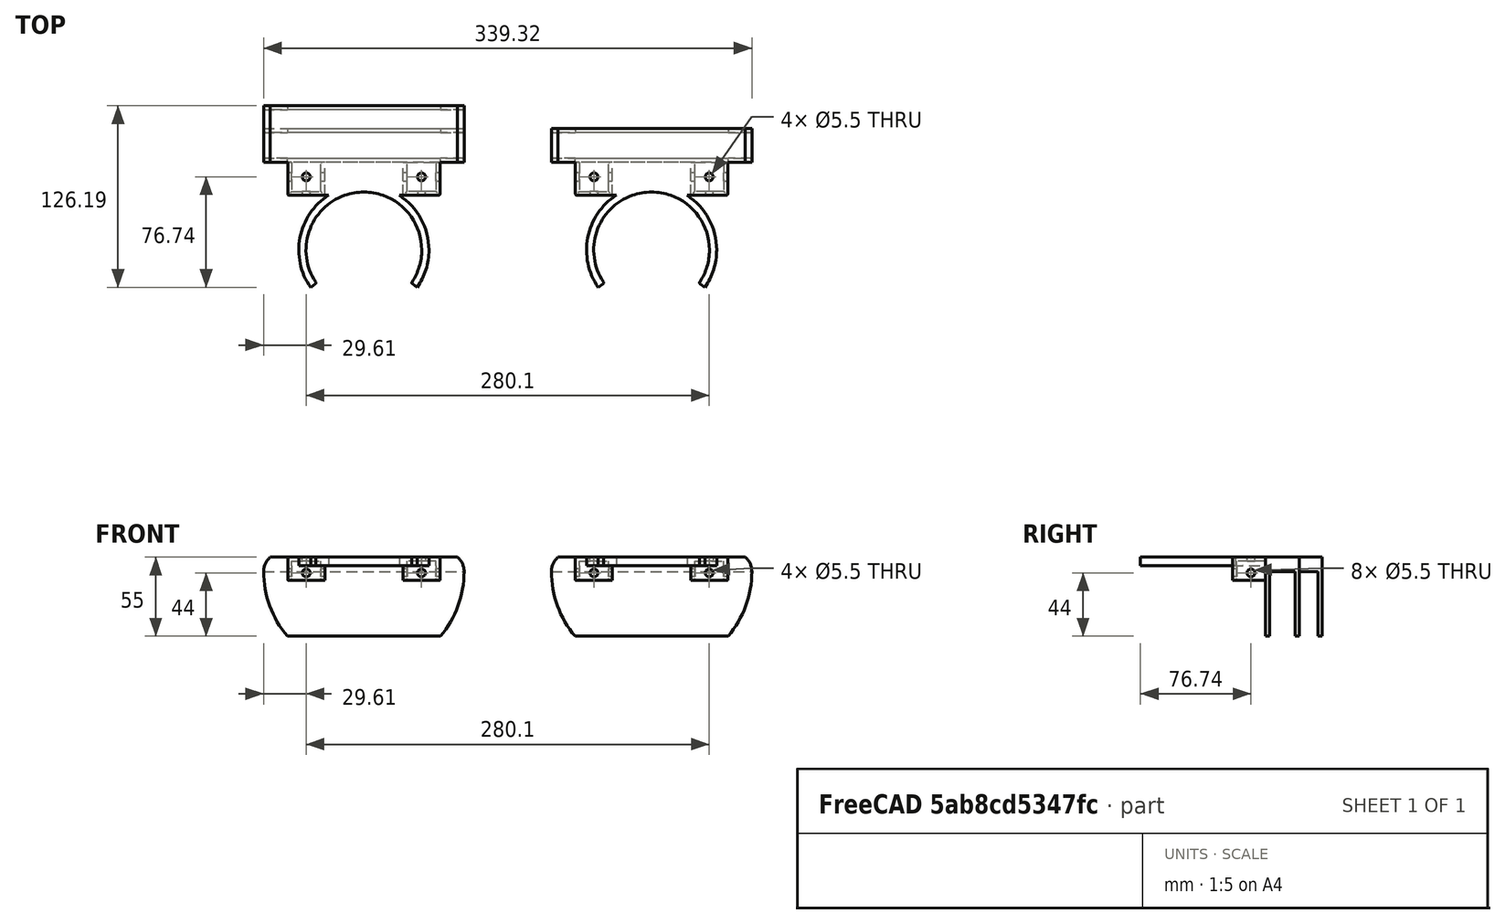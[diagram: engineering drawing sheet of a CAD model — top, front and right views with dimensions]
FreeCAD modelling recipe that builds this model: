
FCSTD DOCUMENT  (FreeCAD 0.19R21775 (Git))
Label: parts - RC1
License: All rights reserved
LicenseURL: http://en.wikipedia.org/wiki/All_rights_reserved
objects: TechDraw::DrawViewDimension×74, Sketcher::SketchObject×20, PartDesign::Pad×12, PartDesign::Pocket×12, TechDraw::DrawViewPart×6, PartDesign::Fillet×4, Spreadsheet::Sheet×2, PartDesign::Body×2, TechDraw::DrawSVGTemplate×2, TechDraw::DrawPage×2, Mesh::Feature×2
note: 78 computed .brp shape members not serialized (recipe doc carries the construction recipe); baked Part::Feature solids carry a one-line shape summary decoded from their .brp

FEATURE [Sketcher::SketchObject] Sketch036
  MapMode = 5
  Support = -> [XY_Plane006]
  expr: Constraints[8] = Spreadsheet006.pillar
  expr: Constraints[6] = Spreadsheet006.pillar / 2 - Spreadsheet006.offset
  expr: Constraints[5] = Spreadsheet006.wall + Spreadsheet006.gap / 2 + Spreadsheet006.extrusion
  expr: Constraints[10] = Spreadsheet006.pillar + 10mm
  sketch-geometry (4):
    g0: LineSegment [constr] StartX=52.9 StartY=0 StartZ=0 EndX=52.9 EndY=-37.955 EndZ=0
    g1: LineSegment [constr] StartX=52.9 StartY=-37.955 StartZ=0 EndX=0 EndY=-37.955 EndZ=0
    g2: Circle CenterX=52.9 CenterY=-37.955 CenterZ=0 NormalX=0 NormalY=0 NormalZ=1 AngleXU=0 Radius=40.225
    g3: Circle CenterX=52.9 CenterY=-37.955 CenterZ=0 NormalX=0 NormalY=0 NormalZ=1 AngleXU=0 Radius=45.225
  constraints (11):
    c: PointOnObject(g0,g-1)
    c: Vertical(g0)
    c: Coincident(g1,g0)
    c: PointOnObject(g1,g-2)
    c: Horizontal(g1)
    c: Distance(g1) = 52.9
    c: Distance(g0) = 37.955
    c: Coincident(g2,g0)
    c: Diameter(g2) = 80.45
    c: Coincident(g3,g2)
    c: Diameter(g3) = 90.45
FEATURE [Sketcher::SketchObject] Sketch038
  MapMode = 5
  Support = -> [XY_Plane006]
  expr: Constraints[25] = Spreadsheet006.wall
  expr: Constraints[26] = Spreadsheet006.wall
  expr: Constraints[28] = Spreadsheet006.wall
  expr: Constraints[29] = Spreadsheet006.wall
  expr: Constraints[27] = Spreadsheet006.wall
  expr: Constraints[30] = Spreadsheet006.gap
  expr: Constraints[31] = Spreadsheet006.extrusion
  sketch-geometry (12):
    g0: LineSegment StartX=0 StartY=0 StartZ=0 EndX=105.8 EndY=0 EndZ=0
    g1: LineSegment StartX=105.8 StartY=0 StartZ=0 EndX=105.8 EndY=25.7 EndZ=0
    g2: LineSegment StartX=105.8 StartY=25.7 StartZ=0 EndX=0 EndY=25.7 EndZ=0
    g3: LineSegment StartX=0 StartY=25.7 StartZ=0 EndX=0 EndY=0 EndZ=0
    g4: LineSegment StartX=2.8 StartY=22.9 StartZ=0 EndX=22.9 EndY=22.9 EndZ=0
    g5: LineSegment StartX=22.9 StartY=22.9 StartZ=0 EndX=22.9 EndY=2.8 EndZ=0
    g6: LineSegment StartX=22.9 StartY=2.8 StartZ=0 EndX=2.8 EndY=2.8 EndZ=0
    g7: LineSegment StartX=2.8 StartY=2.8 StartZ=0 EndX=2.8 EndY=22.9 EndZ=0
    g8: LineSegment StartX=82.9 StartY=22.9 StartZ=0 EndX=103 EndY=22.9 EndZ=0
    g9: LineSegment StartX=103 StartY=22.9 StartZ=0 EndX=103 EndY=2.8 EndZ=0
    g10: LineSegment StartX=103 StartY=2.8 StartZ=0 EndX=82.9 EndY=2.8 EndZ=0
    g11: LineSegment StartX=82.9 StartY=2.8 StartZ=0 EndX=82.9 EndY=22.9 EndZ=0
  constraints (35):
    c: Coincident(g0,g1)
    c: Coincident(g1,g2)
    c: Coincident(g2,g3)
    c: Coincident(g3,g0)
    c: Horizontal(g0)
    c: Horizontal(g2)
    c: Vertical(g1)
    c: Vertical(g3)
    c: Coincident(g0,g-1)
    c: Coincident(g4,g5)
    c: Coincident(g5,g6)
    c: Coincident(g6,g7)
    c: Coincident(g7,g4)
    c: Horizontal(g4)
    c: Horizontal(g6)
    c: Vertical(g5)
    c: Vertical(g7)
    c: Coincident(g8,g9)
    c: Coincident(g9,g10)
    c: Coincident(g10,g11)
    c: Coincident(g11,g8)
    c: Horizontal(g8)
    c: Horizontal(g10)
    c: Vertical(g9)
    c: Vertical(g11)
    c: Distance(g5,g0) = 2.8
    c: Distance(g4,g2) = 2.8
    c: Distance(g6,g3) = 2.8
    c: Distance(g8,g2) = 2.8
    c: Distance(g9,g1) = 2.8
    c: Distance(g4,g8) = 60
    c: Distance(g4) = 20.1
    c: Equal(g4,g5)
    c: Equal(g5,g11)
    c: Equal(g4,g8)
FEATURE [PartDesign::Pad] Pad020
  Length = 6
  Length2 = 100
  Profile = -> Sketch038
  Type = 0
  expr: Length = Spreadsheet006.height
FEATURE [PartDesign::Pad] Pad019
  BaseFeature = -> Pad020
  Length = 6
  Length2 = 100
  Profile = -> Sketch036
  Type = 0
  expr: Length = Spreadsheet006.height
FEATURE [PartDesign::Pocket] Pocket020
  BaseFeature = -> Pad019
  Length = 6
  Length2 = 100
  Profile = -> Pad019 [Face25]
  Type = 0
  expr: Length = Spreadsheet006.height
FEATURE [Spreadsheet::Sheet] Spreadsheet006  label="Data Laptop Holder - One Slot Closed"
  cells = A1=Extrusion width; B1(extrusion)==20.1mm; A2=wall thinkness; B2(wall)==2.8mm; A3=Gap; B3(gap)==60mm; A4=height; B4(height)==6mm; A5=Pillar; B5(pillar)==80.45mm; A6=offset; B6(offset)==2.27mm; A7=cake; B7(cake)==110deg; A8=Socket Height; B8(socketheight)==10mm; A9=Fix Hole Diameter; B9(fixholedia)==5.5mm; A10=Block; A11=Depth; B11(block_depth)==gap + 70mm; A12=Laptop Height; B12(block_mbp)==18mm; C12=Adjust laptop height here; A13=Overhang; B13(block_overhang)==50deg; A14=Support Sidewall; B14(block_sidewall)==3mm; A15=New Height; B15(block_height)==10mm; A16=New Support Height; B16(block_newsupportheight)==45mm
FEATURE [Sketcher::SketchObject] Sketch039
  MapMode = 5
  Support = -> [XY_Plane006]
  expr: Constraints[5] = Spreadsheet006.pillar / 2 - Spreadsheet006.offset
  expr: Constraints[6] = Spreadsheet006.wall + Spreadsheet006.extrusion + Spreadsheet006.gap / 2
  expr: Constraints[14] = Spreadsheet006.cake / 2
  expr: Constraints[7] = Spreadsheet006.pillar + 20mm
  expr: Constraints[19] = Spreadsheet006.cake
  sketch-geometry (7):
    g0: LineSegment [constr] StartX=52.9 StartY=0 StartZ=0 EndX=52.9 EndY=-37.955 EndZ=0
    g1: LineSegment [constr] StartX=52.9 StartY=-37.955 StartZ=0 EndX=0 EndY=-37.955 EndZ=0
    g2: Circle [constr] CenterX=52.9 CenterY=-37.955 CenterZ=0 NormalX=0 NormalY=0 NormalZ=1 AngleXU=0 Radius=50.225
    g3: LineSegment [constr] StartX=52.9 StartY=-37.955 StartZ=0 EndX=52.9 EndY=-88.18 EndZ=0
    g4: LineSegment StartX=52.9 StartY=-37.955 StartZ=0 EndX=94.0419 EndY=-66.7629 EndZ=0
    g5: LineSegment StartX=52.9 StartY=-37.955 StartZ=0 EndX=11.7581 EndY=-66.7629 EndZ=0
    g6: ArcOfCircle CenterX=52.9 CenterY=-37.955 CenterZ=0 NormalX=0 NormalY=0 NormalZ=1 AngleXU=0 Radius=50.225 StartAngle=3.75246 EndAngle=5.67232
  constraints (20):
    c: PointOnObject(g0,g-1)
    c: Vertical(g0)
    c: Coincident(g1,g0)
    c: PointOnObject(g1,g-2)
    c: Horizontal(g1)
    c: Distance(g0) = 37.955
    c: Distance(g1) = 52.9
    c: Diameter(g2) = 100.45
    c: Coincident(g2,g0)
    c: Coincident(g3,g0)
    c: PointOnObject(g3,g2)
    c: Vertical(g3)
    c: Coincident(g4,g0)
    c: PointOnObject(g4,g2)
    c: Angle(g3,g4) = 0.959931
    c: Coincident(g5,g4)
    c: Coincident(g6,g4)
    c: Coincident(g6,g4)
    c: Coincident(g6,g5)
    c: Angle(g5,g4) = 1.91986
FEATURE [PartDesign::Pocket] Pocket021
  BaseFeature = -> Pocket020
  Length = 6
  Length2 = 100
  Profile = -> Sketch039
  Reversed = true
  Type = 0
  expr: Length = Spreadsheet006.height
FEATURE [PartDesign::Fillet] Fillet008
  Base = -> Pocket021 [Edge51,Edge71]
  BaseFeature = -> Pocket021
  Radius = 1
  SupportTransform = true
FEATURE [Sketcher::SketchObject] Sketch034
  ExternalGeometry = -> [Fillet008]
  MapMode = 5
  Placement = pos=(0,0,0) rot=(1,0,0;3.14159rad)
  Support = -> [Fillet008]
  expr: Constraints[40] = Spreadsheet006.wall * 2 + Spreadsheet006.extrusion
  expr: Constraints[41] = Spreadsheet006.wall * 2 + Spreadsheet006.extrusion
  sketch-geometry (16):
    g0: LineSegment StartX=2.8 StartY=-2.8 StartZ=0 EndX=22.9 EndY=-2.8 EndZ=0
    g1: LineSegment StartX=22.9 StartY=-2.8 StartZ=0 EndX=22.9 EndY=-22.9 EndZ=0
    g2: LineSegment StartX=22.9 StartY=-22.9 StartZ=0 EndX=2.8 EndY=-22.9 EndZ=0
    g3: LineSegment StartX=2.8 StartY=-22.9 StartZ=0 EndX=2.8 EndY=-2.8 EndZ=0
    g4: LineSegment StartX=82.9 StartY=-22.9 StartZ=0 EndX=103 EndY=-22.9 EndZ=0
    g5: LineSegment StartX=103 StartY=-22.9 StartZ=0 EndX=103 EndY=-2.8 EndZ=0
    g6: LineSegment StartX=103 StartY=-2.8 StartZ=0 EndX=82.9 EndY=-2.8 EndZ=0
    g7: LineSegment StartX=82.9 StartY=-2.8 StartZ=0 EndX=82.9 EndY=-22.9 EndZ=0
    g8: LineSegment StartX=0 StartY=0 StartZ=0 EndX=25.7 EndY=0 EndZ=0
    g9: LineSegment StartX=25.7 StartY=0 StartZ=0 EndX=25.7 EndY=-25.7 EndZ=0
    g10: LineSegment StartX=25.7 StartY=-25.7 StartZ=0 EndX=0 EndY=-25.7 EndZ=0
    g11: LineSegment StartX=0 StartY=-25.7 StartZ=0 EndX=0 EndY=0 EndZ=0
    g12: LineSegment StartX=105.8 StartY=0 StartZ=0 EndX=80.1 EndY=0 EndZ=0
    g13: LineSegment StartX=80.1 StartY=0 StartZ=0 EndX=80.1 EndY=-25.7 EndZ=0
    g14: LineSegment StartX=80.1 StartY=-25.7 StartZ=0 EndX=105.8 EndY=-25.7 EndZ=0
    g15: LineSegment StartX=105.8 StartY=-25.7 StartZ=0 EndX=105.8 EndY=0 EndZ=0
  constraints (42):
    c: Coincident(g0,g1)
    c: Coincident(g1,g2)
    c: Coincident(g2,g3)
    c: Coincident(g3,g0)
    c: Horizontal(g0)
    c: Horizontal(g2)
    c: Vertical(g1)
    c: Vertical(g3)
    c: Coincident(g0,g-6)
    c: Coincident(g1,g-7)
    c: Coincident(g4,g5)
    c: Coincident(g5,g6)
    c: Coincident(g6,g7)
    c: Coincident(g7,g4)
    c: Horizontal(g4)
    c: Horizontal(g6)
    c: Vertical(g5)
    c: Vertical(g7)
    c: Coincident(g4,g-4)
    c: Coincident(g5,g-3)
    c: Coincident(g8,g9)
    c: Coincident(g9,g10)
    c: Coincident(g10,g11)
    c: Coincident(g11,g8)
    c: Horizontal(g8)
    c: Horizontal(g10)
    c: Vertical(g9)
    c: Vertical(g11)
    c: Coincident(g8,g-1)
    c: PointOnObject(g9,g-8)
    c: Coincident(g12,g13)
    c: Coincident(g13,g14)
    c: Coincident(g14,g15)
    c: Coincident(g15,g12)
    c: Horizontal(g12)
    c: Horizontal(g14)
    c: Vertical(g13)
    c: Vertical(g15)
    c: Coincident(g12,g-5)
    c: PointOnObject(g13,g-8)
    c: Distance(g10) = 25.7
    c: Distance(g14) = 25.7
FEATURE [PartDesign::Pad] Pad021
  BaseFeature = -> Fillet008
  Length = 10
  Length2 = 100
  Profile = -> Sketch034
  Type = 0
  expr: Length = Spreadsheet006.socketheight
FEATURE [Sketcher::SketchObject] Sketch033
  ExternalGeometry = -> [Pad021]
  MapMode = 5
  Placement = pos=(0,0,0) rot=(0.57735,-0.57735,-0.57735;2.0944rad)
  Support = -> [Pad021]
  expr: Constraints[0] = Spreadsheet006.wall + 0.5 * Spreadsheet006.extrusion
  expr: Constraints[1] = Spreadsheet006.socketheight / 2
  expr: Constraints[2] = Spreadsheet006.fixholedia
  sketch-geometry (1):
    g0: Circle CenterX=-12.85 CenterY=-5 CenterZ=0 NormalX=0 NormalY=0 NormalZ=1 AngleXU=0 Radius=2.75
  constraints (3):
    c: Distance(g0,g-4) = 12.85
    c: Distance(g0,g-3) = 5
    c: Diameter(g0) = 5.5
FEATURE [PartDesign::Pocket] Pocket024
  BaseFeature = -> Pad021
  Length = 105.8
  Length2 = 100
  Profile = -> Sketch033
  Type = 0
  expr: Length = Spreadsheet006.gap + 2 * (Spreadsheet006.wall + Spreadsheet006.extrusion)
FEATURE [Sketcher::SketchObject] Sketch040
  ExternalGeometry = -> [Pocket024]
  MapMode = 5
  Placement = pos=(0,0,0) rot=(1,0,0;1.5708rad)
  Support = -> [Pocket024]
  expr: Constraints[0] = Spreadsheet006.wall + 0.5 * Spreadsheet006.extrusion
  expr: Constraints[1] = Spreadsheet006.wall + 0.5 * Spreadsheet006.extrusion
  expr: Constraints[3] = Spreadsheet006.socketheight / 2
  expr: Constraints[2] = Spreadsheet006.socketheight / 2
  expr: Constraints[4] = Spreadsheet006.fixholedia
  sketch-geometry (2):
    g0: Circle CenterX=12.85 CenterY=-5 CenterZ=0 NormalX=0 NormalY=0 NormalZ=1 AngleXU=0 Radius=2.75
    g1: Circle CenterX=92.95 CenterY=-5 CenterZ=0 NormalX=0 NormalY=0 NormalZ=1 AngleXU=0 Radius=2.75
  constraints (6):
    c: Distance(g0,g-5) = 12.85
    c: Distance(g1,g-4) = 12.85
    c: Distance(g0,g-6) = 5
    c: Distance(g1,g-3) = 5
    c: Diameter(g0) = 5.5
    c: Equal(g0,g1)
FEATURE [PartDesign::Pocket] Pocket023
  BaseFeature = -> Pocket024
  Length = 2.8
  Length2 = 100
  Profile = -> Sketch040
  Type = 0
  expr: Length = Spreadsheet006.wall
FEATURE [PartDesign::Fillet] Fillet009
  Base = -> Pocket023 [Edge114,Edge113,Edge112,Edge85,Edge86,Edge83,Edge37,Edge22,Edge108,Edge70]
  BaseFeature = -> Pocket023
  Radius = 1
  SupportTransform = true
FEATURE [Sketcher::SketchObject] Sketch037
  ExternalGeometry = -> [Fillet009]
  MapMode = 5
  Placement = pos=(0,25.7,0) rot=(0,0.707107,0.707107;3.14159rad)
  Support = -> [Fillet009]
  expr: Constraints[7] = Spreadsheet006.block_depth / 2
  expr: Constraints[5] = Spreadsheet006.block_height
  expr: Constraints[16] = 180deg - Spreadsheet006.block_overhang
  expr: Constraints[10] = 180deg - Spreadsheet006.block_overhang
  expr: Constraints[3] = (Spreadsheet006.block_depth - (Spreadsheet006.gap + 2 * (Spreadsheet006.wall + Spreadsheet006.extrusion))) / 2
  expr: Constraints[6] = 2 * Spreadsheet006.block_depth
  expr: Constraints[2] = Spreadsheet006.block_depth
  sketch-geometry (7):
    g0: LineSegment StartX=12.1 StartY=6 StartZ=0 EndX=-117.9 EndY=6 EndZ=0
    g1: LineSegment [constr] StartX=-182.9 StartY=-4 StartZ=0 EndX=77.1 EndY=-4 EndZ=0
    g2: LineSegment [constr] StartX=-117.9 StartY=6 StartZ=0 EndX=-109.509 EndY=-4 EndZ=0
    g3: ArcOfCircle CenterX=-109.509 CenterY=-4 CenterZ=0 NormalX=0 NormalY=0 NormalZ=1 AngleXU=0 Radius=13.0541 StartAngle=2.26893 EndAngle=3.14159
    g4: LineSegment [constr] StartX=12.1 StartY=6 StartZ=0 EndX=3.709 EndY=-4 EndZ=0
    g5: ArcOfCircle CenterX=3.709 CenterY=-4 CenterZ=0 NormalX=0 NormalY=0 NormalZ=1 AngleXU=0 Radius=13.0541 StartAngle=2.9155e-12 EndAngle=0.872665
    g6: ArcOfCircle CenterX=-52.9 CenterY=-4 CenterZ=0 NormalX=0 NormalY=0 NormalZ=1 AngleXU=0 Radius=69.6631 StartAngle=3.14159 EndAngle=6.28319
  constraints (23):
    c: Horizontal(g0)
    c: PointOnObject(g-4,g0)
    c: Distance(g0) = 130
    c: Distance(g0,g-5) = 12.1
    c: Horizontal(g1)
    c: Distance(g0,g1) = 10
    c: Distance(g1) = 260
    c: DistanceX(g1,g0) = 65
    c: Coincident(g2,g0)
    c: PointOnObject(g2,g1)
    c: Angle(g1,g2) = 2.26893
    c: Coincident(g3,g2)
    c: Coincident(g3,g0)
    c: PointOnObject(g3,g1)
    c: Coincident(g4,g0)
    c: PointOnObject(g4,g1)
    c: Angle(g4,g1) = 2.26893
    c: Coincident(g5,g4)
    c: Coincident(g5,g0)
    c: PointOnObject(g5,g1)
    c: PointOnObject(g6,g1)
    c: Coincident(g6,g3)
    c: Coincident(g6,g5)
FEATURE [PartDesign::Pad] Pad022
  BaseFeature = -> Fillet009
  Length = 20.8
  Length2 = 100
  Profile = -> Sketch037
  Type = 0
  expr: Length = Spreadsheet006.block_mbp + Spreadsheet006.wall
FEATURE [PartDesign::Pad] Pad018
  BaseFeature = -> Pad022
  Length = 2.8
  Length2 = 100
  Profile = -> Pad022 [Face4]
  Type = 0
  expr: Length = Spreadsheet006.wall
FEATURE [Sketcher::SketchObject] Sketch041
  AttachmentOffset = pos=(0,0,-49) rot=(0,0,1;0rad)
  ExternalGeometry = -> [Pad018]
  MapMode = 5
  Placement = pos=(0,0,-49) rot=(0,0,1;0rad)
  Support = -> [XY_Plane006]
  expr: .AttachmentOffset.Base.z = -1 * (Spreadsheet006.block_newsupportheight + Spreadsheet006.block_height - Spreadsheet006.height)
  sketch-geometry (4):
    g0: LineSegment StartX=-16.7631 StartY=46.5 StartZ=0 EndX=122.563 EndY=46.5 EndZ=0
    g1: LineSegment StartX=122.563 StartY=46.5 StartZ=0 EndX=122.563 EndY=0 EndZ=0
    g2: LineSegment StartX=122.563 StartY=0 StartZ=0 EndX=-16.7631 EndY=0 EndZ=0
    g3: LineSegment StartX=-16.7631 StartY=0 StartZ=0 EndX=-16.7631 EndY=46.5 EndZ=0
  constraints (10):
    c: Coincident(g0,g1)
    c: Coincident(g1,g2)
    c: Coincident(g2,g3)
    c: Coincident(g3,g0)
    c: Horizontal(g2)
    c: Vertical(g1)
    c: Vertical(g3)
    c: Coincident(g0,g-5)
    c: PointOnObject(g1,g-1)
    c: Coincident(g-6,g0)
FEATURE [PartDesign::Pocket] Pocket025
  BaseFeature = -> Pad018
  Length = 61
  Length2 = 100
  Profile = -> Sketch041
  Type = 0
  expr: Length = Spreadsheet006.height + Spreadsheet006.block_newsupportheight + Spreadsheet006.block_height
FEATURE [Sketcher::SketchObject] Sketch035
  ExternalGeometry = -> [Pocket025]
  MapMode = 5
  Placement = pos=(0,0,-49) rot=(1,0,0;3.14159rad)
  Support = -> [Pocket025]
  expr: Constraints[11] = Spreadsheet006.block_mbp
  expr: Constraints[10] = Spreadsheet006.wall
  sketch-geometry (4):
    g0: LineSegment StartX=-16.7631 StartY=-25.7 StartZ=0 EndX=122.563 EndY=-25.7 EndZ=0
    g1: LineSegment StartX=122.563 StartY=-25.7 StartZ=0 EndX=122.563 EndY=-43.7 EndZ=0
    g2: LineSegment StartX=122.563 StartY=-43.7 StartZ=0 EndX=-16.7631 EndY=-43.7 EndZ=0
    g3: LineSegment StartX=-16.7631 StartY=-43.7 StartZ=0 EndX=-16.7631 EndY=-25.7 EndZ=0
  constraints (12):
    c: Coincident(g0,g1)
    c: Coincident(g1,g2)
    c: Coincident(g2,g3)
    c: Coincident(g3,g0)
    c: Horizontal(g0)
    c: Horizontal(g2)
    c: Vertical(g1)
    c: Vertical(g3)
    c: PointOnObject(g0,g-3)
    c: PointOnObject(g1,g-4)
    c: Distance(g-5,g0) = 2.8
    c: Distance(g1) = 18
FEATURE [PartDesign::Pocket] Pocket022
  BaseFeature = -> Pocket025
  Length = 45
  Length2 = 100
  Profile = -> Sketch035
  Type = 0
  expr: Length = Spreadsheet006.block_newsupportheight
FEATURE [Sketcher::SketchObject] Sketch043
  MapMode = 5
  Support = -> [XY_Plane007]
  expr: Constraints[10] = Spreadsheet007.pillar + 10mm
  expr: Constraints[5] = Spreadsheet007.wall + Spreadsheet007.gap / 2 + Spreadsheet007.extrusion
  expr: Constraints[6] = Spreadsheet007.pillar / 2 - Spreadsheet007.offset
  expr: Constraints[8] = Spreadsheet007.pillar
  sketch-geometry (4):
    g0: LineSegment [constr] StartX=52.9 StartY=0 StartZ=0 EndX=52.9 EndY=-37.955 EndZ=0
    g1: LineSegment [constr] StartX=52.9 StartY=-37.955 StartZ=0 EndX=0 EndY=-37.955 EndZ=0
    g2: Circle CenterX=52.9 CenterY=-37.955 CenterZ=0 NormalX=0 NormalY=0 NormalZ=1 AngleXU=0 Radius=40.225
    g3: Circle CenterX=52.9 CenterY=-37.955 CenterZ=0 NormalX=0 NormalY=0 NormalZ=1 AngleXU=0 Radius=45.225
  constraints (11):
    c: PointOnObject(g0,g-1)
    c: Vertical(g0)
    c: Coincident(g1,g0)
    c: PointOnObject(g1,g-2)
    c: Horizontal(g1)
    c: Distance(g1) = 52.9
    c: Distance(g0) = 37.955
    c: Coincident(g2,g0)
    c: Diameter(g2) = 80.45
    c: Coincident(g3,g2)
    c: Diameter(g3) = 90.45
FEATURE [Sketcher::SketchObject] Sketch047
  MapMode = 5
  Support = -> [XY_Plane007]
  expr: Constraints[31] = Spreadsheet007.extrusion
  expr: Constraints[30] = Spreadsheet007.gap
  expr: Constraints[27] = Spreadsheet007.wall
  expr: Constraints[29] = Spreadsheet007.wall
  expr: Constraints[28] = Spreadsheet007.wall
  expr: Constraints[26] = Spreadsheet007.wall
  expr: Constraints[25] = Spreadsheet007.wall
  sketch-geometry (12):
    g0: LineSegment StartX=0 StartY=0 StartZ=0 EndX=105.8 EndY=0 EndZ=0
    g1: LineSegment StartX=105.8 StartY=0 StartZ=0 EndX=105.8 EndY=25.7 EndZ=0
    g2: LineSegment StartX=105.8 StartY=25.7 StartZ=0 EndX=0 EndY=25.7 EndZ=0
    g3: LineSegment StartX=0 StartY=25.7 StartZ=0 EndX=0 EndY=0 EndZ=0
    g4: LineSegment StartX=2.8 StartY=22.9 StartZ=0 EndX=22.9 EndY=22.9 EndZ=0
    g5: LineSegment StartX=22.9 StartY=22.9 StartZ=0 EndX=22.9 EndY=2.8 EndZ=0
    g6: LineSegment StartX=22.9 StartY=2.8 StartZ=0 EndX=2.8 EndY=2.8 EndZ=0
    g7: LineSegment StartX=2.8 StartY=2.8 StartZ=0 EndX=2.8 EndY=22.9 EndZ=0
    g8: LineSegment StartX=82.9 StartY=22.9 StartZ=0 EndX=103 EndY=22.9 EndZ=0
    g9: LineSegment StartX=103 StartY=22.9 StartZ=0 EndX=103 EndY=2.8 EndZ=0
    g10: LineSegment StartX=103 StartY=2.8 StartZ=0 EndX=82.9 EndY=2.8 EndZ=0
    g11: LineSegment StartX=82.9 StartY=2.8 StartZ=0 EndX=82.9 EndY=22.9 EndZ=0
  constraints (35):
    c: Coincident(g0,g1)
    c: Coincident(g1,g2)
    c: Coincident(g2,g3)
    c: Coincident(g3,g0)
    c: Horizontal(g0)
    c: Horizontal(g2)
    c: Vertical(g1)
    c: Vertical(g3)
    c: Coincident(g0,g-1)
    c: Coincident(g4,g5)
    c: Coincident(g5,g6)
    c: Coincident(g6,g7)
    c: Coincident(g7,g4)
    c: Horizontal(g4)
    c: Horizontal(g6)
    c: Vertical(g5)
    c: Vertical(g7)
    c: Coincident(g8,g9)
    c: Coincident(g9,g10)
    c: Coincident(g10,g11)
    c: Coincident(g11,g8)
    c: Horizontal(g8)
    c: Horizontal(g10)
    c: Vertical(g9)
    c: Vertical(g11)
    c: Distance(g5,g0) = 2.8
    c: Distance(g4,g2) = 2.8
    c: Distance(g6,g3) = 2.8
    c: Distance(g8,g2) = 2.8
    c: Distance(g9,g1) = 2.8
    c: Distance(g4,g8) = 60
    c: Distance(g4) = 20.1
    c: Equal(g4,g5)
    c: Equal(g5,g11)
    c: Equal(g4,g8)
FEATURE [PartDesign::Pad] Pad026
  Length = 6
  Length2 = 100
  Profile = -> Sketch047
  Type = 0
  expr: Length = Spreadsheet007.height
FEATURE [Spreadsheet::Sheet] Spreadsheet007  label="Data Laptop Holder - Two Slots - Closed"
  cells = A1=Extrusion width; B1(extrusion)==20.1mm; A2=wall thinkness; B2(wall)==2.8mm; A3=Gap; B3(gap)==60mm; A4=height; B4(height)==6mm; A5=Pillar; B5(pillar)==80.45mm; A6=offset; B6(offset)==2.27mm; A7=cake; B7(cake)==110deg; A8=Socket Height; B8(socketheight)==10mm; A9=Fix Hole Diameter; B9(fixholedia)==5.5mm; A10=Block; A11=Depth; B11(block_depth)==gap + 70mm; A12=Inner Laptop Height; B12(block_mbp)==18mm; C12=<-----; D12=Adjust inner laptop height here; A13=Outer Laptop Height; B13(block_mba)==13mm; C13=<-----; D13=Adjust outer laptop height here; A14=Overhang; B14(block_overhang)==50deg; A15=Support Sidewall; B15(block_sidewall)==3mm; A16=New Height; B16(block_height)==10mm; A17=New Support Height; B17(block_newsupportheight)==45mm
FEATURE [PartDesign::Pad] Pad027
  BaseFeature = -> Pad026
  Length = 6
  Length2 = 100
  Profile = -> Sketch043
  Type = 0
  expr: Length = Spreadsheet007.height
FEATURE [PartDesign::Pocket] Pocket028
  BaseFeature = -> Pad027
  Length = 6
  Length2 = 100
  Profile = -> Pad027 [Face25]
  Type = 0
  expr: Length = Spreadsheet007.height
FEATURE [Sketcher::SketchObject] Sketch050
  MapMode = 5
  Support = -> [XY_Plane007]
  expr: Constraints[19] = Spreadsheet007.cake
  expr: Constraints[7] = Spreadsheet007.pillar + 20mm
  expr: Constraints[14] = Spreadsheet007.cake / 2
  expr: Constraints[6] = Spreadsheet007.wall + Spreadsheet007.extrusion + Spreadsheet007.gap / 2
  expr: Constraints[5] = Spreadsheet007.pillar / 2 - Spreadsheet007.offset
  sketch-geometry (7):
    g0: LineSegment [constr] StartX=52.9 StartY=0 StartZ=0 EndX=52.9 EndY=-37.955 EndZ=0
    g1: LineSegment [constr] StartX=52.9 StartY=-37.955 StartZ=0 EndX=0 EndY=-37.955 EndZ=0
    g2: Circle [constr] CenterX=52.9 CenterY=-37.955 CenterZ=0 NormalX=0 NormalY=0 NormalZ=1 AngleXU=0 Radius=50.225
    g3: LineSegment [constr] StartX=52.9 StartY=-37.955 StartZ=0 EndX=52.9 EndY=-88.18 EndZ=0
    g4: LineSegment StartX=52.9 StartY=-37.955 StartZ=0 EndX=94.0419 EndY=-66.7629 EndZ=0
    g5: LineSegment StartX=52.9 StartY=-37.955 StartZ=0 EndX=11.7581 EndY=-66.7629 EndZ=0
    g6: ArcOfCircle CenterX=52.9 CenterY=-37.955 CenterZ=0 NormalX=0 NormalY=0 NormalZ=1 AngleXU=0 Radius=50.225 StartAngle=3.75246 EndAngle=5.67232
  constraints (20):
    c: PointOnObject(g0,g-1)
    c: Vertical(g0)
    c: Coincident(g1,g0)
    c: PointOnObject(g1,g-2)
    c: Horizontal(g1)
    c: Distance(g0) = 37.955
    c: Distance(g1) = 52.9
    c: Diameter(g2) = 100.45
    c: Coincident(g2,g0)
    c: Coincident(g3,g0)
    c: PointOnObject(g3,g2)
    c: Vertical(g3)
    c: Coincident(g4,g0)
    c: PointOnObject(g4,g2)
    c: Angle(g3,g4) = 0.959931
    c: Coincident(g5,g4)
    c: Coincident(g6,g4)
    c: Coincident(g6,g4)
    c: Coincident(g6,g5)
    c: Angle(g5,g4) = 1.91986
FEATURE [PartDesign::Pocket] Pocket026
  BaseFeature = -> Pocket028
  Length = 6
  Length2 = 100
  Profile = -> Sketch050
  Reversed = true
  Type = 0
  expr: Length = Spreadsheet007.height
FEATURE [PartDesign::Fillet] Fillet011
  Base = -> Pocket026 [Edge51,Edge71]
  BaseFeature = -> Pocket026
  Radius = 1
  SupportTransform = true
FEATURE [Sketcher::SketchObject] Sketch049
  ExternalGeometry = -> [Fillet011]
  MapMode = 5
  Placement = pos=(0,0,0) rot=(1,0,0;3.14159rad)
  Support = -> [Fillet011]
  expr: Constraints[41] = Spreadsheet007.wall * 2 + Spreadsheet007.extrusion
  expr: Constraints[40] = Spreadsheet007.wall * 2 + Spreadsheet007.extrusion
  sketch-geometry (16):
    g0: LineSegment StartX=2.8 StartY=-2.8 StartZ=0 EndX=22.9 EndY=-2.8 EndZ=0
    g1: LineSegment StartX=22.9 StartY=-2.8 StartZ=0 EndX=22.9 EndY=-22.9 EndZ=0
    g2: LineSegment StartX=22.9 StartY=-22.9 StartZ=0 EndX=2.8 EndY=-22.9 EndZ=0
    g3: LineSegment StartX=2.8 StartY=-22.9 StartZ=0 EndX=2.8 EndY=-2.8 EndZ=0
    g4: LineSegment StartX=82.9 StartY=-22.9 StartZ=0 EndX=103 EndY=-22.9 EndZ=0
    g5: LineSegment StartX=103 StartY=-22.9 StartZ=0 EndX=103 EndY=-2.8 EndZ=0
    g6: LineSegment StartX=103 StartY=-2.8 StartZ=0 EndX=82.9 EndY=-2.8 EndZ=0
    g7: LineSegment StartX=82.9 StartY=-2.8 StartZ=0 EndX=82.9 EndY=-22.9 EndZ=0
    g8: LineSegment StartX=0 StartY=0 StartZ=0 EndX=25.7 EndY=0 EndZ=0
    g9: LineSegment StartX=25.7 StartY=0 StartZ=0 EndX=25.7 EndY=-25.7 EndZ=0
    g10: LineSegment StartX=25.7 StartY=-25.7 StartZ=0 EndX=0 EndY=-25.7 EndZ=0
    g11: LineSegment StartX=0 StartY=-25.7 StartZ=0 EndX=0 EndY=0 EndZ=0
    g12: LineSegment StartX=105.8 StartY=0 StartZ=0 EndX=80.1 EndY=0 EndZ=0
    g13: LineSegment StartX=80.1 StartY=0 StartZ=0 EndX=80.1 EndY=-25.7 EndZ=0
    g14: LineSegment StartX=80.1 StartY=-25.7 StartZ=0 EndX=105.8 EndY=-25.7 EndZ=0
    g15: LineSegment StartX=105.8 StartY=-25.7 StartZ=0 EndX=105.8 EndY=0 EndZ=0
  constraints (42):
    c: Coincident(g0,g1)
    c: Coincident(g1,g2)
    c: Coincident(g2,g3)
    c: Coincident(g3,g0)
    c: Horizontal(g0)
    c: Horizontal(g2)
    c: Vertical(g1)
    c: Vertical(g3)
    c: Coincident(g0,g-6)
    c: Coincident(g1,g-7)
    c: Coincident(g4,g5)
    c: Coincident(g5,g6)
    c: Coincident(g6,g7)
    c: Coincident(g7,g4)
    c: Horizontal(g4)
    c: Horizontal(g6)
    c: Vertical(g5)
    c: Vertical(g7)
    c: Coincident(g4,g-4)
    c: Coincident(g5,g-3)
    c: Coincident(g8,g9)
    c: Coincident(g9,g10)
    c: Coincident(g10,g11)
    c: Coincident(g11,g8)
    c: Horizontal(g8)
    c: Horizontal(g10)
    c: Vertical(g9)
    c: Vertical(g11)
    c: Coincident(g8,g-1)
    c: PointOnObject(g9,g-8)
    c: Coincident(g12,g13)
    c: Coincident(g13,g14)
    c: Coincident(g14,g15)
    c: Coincident(g15,g12)
    c: Horizontal(g12)
    c: Horizontal(g14)
    c: Vertical(g13)
    c: Vertical(g15)
    c: Coincident(g12,g-5)
    c: PointOnObject(g13,g-8)
    c: Distance(g10) = 25.7
    c: Distance(g14) = 25.7
FEATURE [PartDesign::Pad] Pad023
  BaseFeature = -> Fillet011
  Length = 10
  Length2 = 100
  Profile = -> Sketch049
  Type = 0
  expr: Length = Spreadsheet007.socketheight
FEATURE [Sketcher::SketchObject] Sketch045
  ExternalGeometry = -> [Pad023]
  MapMode = 5
  Placement = pos=(0,0,0) rot=(0.57735,-0.57735,-0.57735;2.0944rad)
  Support = -> [Pad023]
  expr: Constraints[2] = Spreadsheet007.fixholedia
  expr: Constraints[1] = Spreadsheet007.socketheight / 2
  expr: Constraints[0] = Spreadsheet007.wall + 0.5 * Spreadsheet007.extrusion
  sketch-geometry (1):
    g0: Circle CenterX=-12.85 CenterY=-5 CenterZ=0 NormalX=0 NormalY=0 NormalZ=1 AngleXU=0 Radius=2.75
  constraints (3):
    c: Distance(g0,g-4) = 12.85
    c: Distance(g0,g-3) = 5
    c: Diameter(g0) = 5.5
FEATURE [PartDesign::Pocket] Pocket031
  BaseFeature = -> Pad023
  Length = 105.8
  Length2 = 100
  Profile = -> Sketch045
  Type = 0
  expr: Length = Spreadsheet007.gap + 2 * (Spreadsheet007.wall + Spreadsheet007.extrusion)
FEATURE [Sketcher::SketchObject] Sketch042
  ExternalGeometry = -> [Pocket031]
  MapMode = 5
  Placement = pos=(0,0,0) rot=(1,0,0;1.5708rad)
  Support = -> [Pocket031]
  expr: Constraints[4] = Spreadsheet007.fixholedia
  expr: Constraints[2] = Spreadsheet007.socketheight / 2
  expr: Constraints[3] = Spreadsheet007.socketheight / 2
  expr: Constraints[1] = Spreadsheet007.wall + 0.5 * Spreadsheet007.extrusion
  expr: Constraints[0] = Spreadsheet007.wall + 0.5 * Spreadsheet007.extrusion
  sketch-geometry (2):
    g0: Circle CenterX=12.85 CenterY=-5 CenterZ=0 NormalX=0 NormalY=0 NormalZ=1 AngleXU=0 Radius=2.75
    g1: Circle CenterX=92.95 CenterY=-5 CenterZ=0 NormalX=0 NormalY=0 NormalZ=1 AngleXU=0 Radius=2.75
  constraints (6):
    c: Distance(g0,g-5) = 12.85
    c: Distance(g1,g-4) = 12.85
    c: Distance(g0,g-6) = 5
    c: Distance(g1,g-3) = 5
    c: Diameter(g0) = 5.5
    c: Equal(g0,g1)
FEATURE [PartDesign::Pocket] Pocket029
  BaseFeature = -> Pocket031
  Length = 2.8
  Length2 = 100
  Profile = -> Sketch042
  Type = 0
  expr: Length = Spreadsheet007.wall
FEATURE [PartDesign::Fillet] Fillet010
  Base = -> Pocket029 [Edge114,Edge113,Edge112,Edge85,Edge86,Edge83,Edge37,Edge22,Edge108,Edge70]
  BaseFeature = -> Pocket029
  Radius = 1
  SupportTransform = true
FEATURE [Sketcher::SketchObject] Sketch046
  ExternalGeometry = -> [Fillet010]
  MapMode = 5
  Placement = pos=(0,25.7,0) rot=(0,0.707107,0.707107;3.14159rad)
  Support = -> [Fillet010]
  expr: Constraints[2] = Spreadsheet007.block_depth
  expr: Constraints[6] = 2 * Spreadsheet007.block_depth
  expr: Constraints[3] = (Spreadsheet007.block_depth - (Spreadsheet007.gap + 2 * (Spreadsheet007.wall + Spreadsheet007.extrusion))) / 2
  expr: Constraints[10] = 180deg - Spreadsheet007.block_overhang
  expr: Constraints[16] = 180deg - Spreadsheet007.block_overhang
  expr: Constraints[5] = Spreadsheet007.block_height
  expr: Constraints[7] = Spreadsheet007.block_depth / 2
  sketch-geometry (7):
    g0: LineSegment StartX=12.1 StartY=6 StartZ=0 EndX=-117.9 EndY=6 EndZ=0
    g1: LineSegment [constr] StartX=-182.9 StartY=-4 StartZ=0 EndX=77.1 EndY=-4 EndZ=0
    g2: LineSegment [constr] StartX=-117.9 StartY=6 StartZ=0 EndX=-109.509 EndY=-4 EndZ=0
    g3: ArcOfCircle CenterX=-109.509 CenterY=-4 CenterZ=0 NormalX=0 NormalY=0 NormalZ=1 AngleXU=0 Radius=13.0541 StartAngle=2.26893 EndAngle=3.14159
    g4: LineSegment [constr] StartX=12.1 StartY=6 StartZ=0 EndX=3.709 EndY=-4 EndZ=0
    g5: ArcOfCircle CenterX=3.709 CenterY=-4 CenterZ=0 NormalX=0 NormalY=0 NormalZ=1 AngleXU=0 Radius=13.0541 StartAngle=2.9155e-12 EndAngle=0.872665
    g6: ArcOfCircle CenterX=-52.9 CenterY=-4 CenterZ=0 NormalX=0 NormalY=0 NormalZ=1 AngleXU=0 Radius=69.6631 StartAngle=3.14159 EndAngle=6.28319
  constraints (23):
    c: Horizontal(g0)
    c: PointOnObject(g-4,g0)
    c: Distance(g0) = 130
    c: Distance(g0,g-5) = 12.1
    c: Horizontal(g1)
    c: Distance(g0,g1) = 10
    c: Distance(g1) = 260
    c: DistanceX(g1,g0) = 65
    c: Coincident(g2,g0)
    c: PointOnObject(g2,g1)
    c: Angle(g1,g2) = 2.26893
    c: Coincident(g3,g2)
    c: Coincident(g3,g0)
    c: PointOnObject(g3,g1)
    c: Coincident(g4,g0)
    c: PointOnObject(g4,g1)
    c: Angle(g4,g1) = 2.26893
    c: Coincident(g5,g4)
    c: Coincident(g5,g0)
    c: PointOnObject(g5,g1)
    c: PointOnObject(g6,g1)
    c: Coincident(g6,g3)
    c: Coincident(g6,g5)
FEATURE [PartDesign::Pad] Pad024
  BaseFeature = -> Fillet010
  Length = 36.6
  Length2 = 100
  Profile = -> Sketch046
  Type = 0
  expr: Length = Spreadsheet007.block_mbp + Spreadsheet007.block_mba + 2 * Spreadsheet007.wall
FEATURE [PartDesign::Pad] Pad025
  BaseFeature = -> Pad024
  Length = 2.8
  Length2 = 100
  Profile = -> Pad024 [Face4]
  Type = 0
  expr: Length = Spreadsheet007.wall
FEATURE [Sketcher::SketchObject] Sketch048
  AttachmentOffset = pos=(0,0,-49) rot=(0,0,1;0rad)
  ExternalGeometry = -> [Pad025]
  MapMode = 5
  Placement = pos=(0,0,-49) rot=(0,0,1;0rad)
  Support = -> [XY_Plane007]
  expr: .AttachmentOffset.Base.z = -1 * (Spreadsheet007.block_newsupportheight + Spreadsheet007.block_height - Spreadsheet007.height)
  sketch-geometry (4):
    g0: LineSegment StartX=-16.7631 StartY=62.3 StartZ=0 EndX=122.563 EndY=62.3 EndZ=0
    g1: LineSegment StartX=122.563 StartY=62.3 StartZ=0 EndX=122.563 EndY=0 EndZ=0
    g2: LineSegment StartX=122.563 StartY=0 StartZ=0 EndX=-16.7631 EndY=0 EndZ=0
    g3: LineSegment StartX=-16.7631 StartY=0 StartZ=0 EndX=-16.7631 EndY=62.3 EndZ=0
  constraints (10):
    c: Coincident(g0,g1)
    c: Coincident(g1,g2)
    c: Coincident(g2,g3)
    c: Coincident(g3,g0)
    c: Horizontal(g2)
    c: Vertical(g1)
    c: Vertical(g3)
    c: Coincident(g0,g-5)
    c: PointOnObject(g1,g-1)
    c: Coincident(g-6,g0)
FEATURE [PartDesign::Pocket] Pocket027
  BaseFeature = -> Pad025
  Length = 61
  Length2 = 100
  Profile = -> Sketch048
  Type = 0
  expr: Length = Spreadsheet007.height + Spreadsheet007.block_newsupportheight + Spreadsheet007.block_height
FEATURE [Sketcher::SketchObject] Sketch044
  ExternalGeometry = -> [Pocket027]
  MapMode = 5
  Placement = pos=(0,0,-49) rot=(1,0,0;3.14159rad)
  Support = -> [Pocket027]
  expr: Constraints[20] = Spreadsheet007.wall
  expr: Constraints[21] = Spreadsheet007.block_mbp
  expr: Constraints[22] = Spreadsheet007.block_mba
  expr: Constraints[23] = Spreadsheet007.wall
  sketch-geometry (8):
    g0: LineSegment StartX=-16.7631 StartY=-25.7 StartZ=0 EndX=122.563 EndY=-25.7 EndZ=0
    g1: LineSegment StartX=122.563 StartY=-25.7 StartZ=0 EndX=122.563 EndY=-43.7 EndZ=0
    g2: LineSegment StartX=122.563 StartY=-43.7 StartZ=0 EndX=-16.7631 EndY=-43.7 EndZ=0
    g3: LineSegment StartX=-16.7631 StartY=-43.7 StartZ=0 EndX=-16.7631 EndY=-25.7 EndZ=0
    g4: LineSegment StartX=-16.7631 StartY=-46.5 StartZ=0 EndX=122.563 EndY=-46.5 EndZ=0
    g5: LineSegment StartX=122.563 StartY=-46.5 StartZ=0 EndX=122.563 EndY=-59.5 EndZ=0
    g6: LineSegment StartX=122.563 StartY=-59.5 StartZ=0 EndX=-16.7631 EndY=-59.5 EndZ=0
    g7: LineSegment StartX=-16.7631 StartY=-59.5 StartZ=0 EndX=-16.7631 EndY=-46.5 EndZ=0
  constraints (24):
    c: Coincident(g0,g1)
    c: Coincident(g1,g2)
    c: Coincident(g2,g3)
    c: Coincident(g3,g0)
    c: Horizontal(g0)
    c: Horizontal(g2)
    c: Vertical(g1)
    c: Vertical(g3)
    c: PointOnObject(g0,g-3)
    c: PointOnObject(g1,g-4)
    c: Coincident(g4,g5)
    c: Coincident(g5,g6)
    c: Coincident(g6,g7)
    c: Coincident(g7,g4)
    c: Horizontal(g4)
    c: Horizontal(g6)
    c: Vertical(g5)
    c: Vertical(g7)
    c: PointOnObject(g4,g-3)
    c: PointOnObject(g5,g-4)
    c: Distance(g-5,g0) = 2.8
    c: Distance(g1) = 18
    c: Distance(g5) = 13
    c: Distance(g2,g4) = 2.8
FEATURE [PartDesign::Pocket] Pocket030
  BaseFeature = -> Pocket027
  Length = 45
  Length2 = 100
  Profile = -> Sketch044
  Type = 0
  expr: Length = Spreadsheet007.block_newsupportheight
FEATURE [Sketcher::SketchObject] Sketch051
  ExternalGeometry = -> [Pocket022]
  MapMode = 5
  Placement = pos=(0,0,6) rot=(0,0,1;0rad)
  Support = -> [Pocket022]
  expr: Constraints[24] = Spreadsheet006.fixholedia
  expr: Constraints[22] = Spreadsheet006.extrusion / 2
  expr: Constraints[23] = Spreadsheet006.extrusion / 2
  expr: Constraints[21] = Spreadsheet006.extrusion / 2
  expr: Constraints[20] = Spreadsheet006.extrusion / 2
  sketch-geometry (10):
    g0: LineSegment StartX=2.8 StartY=22.9 StartZ=0 EndX=22.9 EndY=22.9 EndZ=0
    g1: LineSegment StartX=22.9 StartY=22.9 StartZ=0 EndX=22.9 EndY=2.8 EndZ=0
    g2: LineSegment StartX=22.9 StartY=2.8 StartZ=0 EndX=2.8 EndY=2.8 EndZ=0
    g3: LineSegment StartX=2.8 StartY=2.8 StartZ=0 EndX=2.8 EndY=22.9 EndZ=0
    g4: LineSegment StartX=82.9 StartY=22.9 StartZ=0 EndX=103 EndY=22.9 EndZ=0
    g5: LineSegment StartX=103 StartY=22.9 StartZ=0 EndX=103 EndY=2.8 EndZ=0
    g6: LineSegment StartX=103 StartY=2.8 StartZ=0 EndX=82.9 EndY=2.8 EndZ=0
    g7: LineSegment StartX=82.9 StartY=2.8 StartZ=0 EndX=82.9 EndY=22.9 EndZ=0
    g8: Circle CenterX=12.85 CenterY=12.85 CenterZ=0 NormalX=0 NormalY=0 NormalZ=1 AngleXU=0 Radius=2.75
    g9: Circle CenterX=92.95 CenterY=12.85 CenterZ=0 NormalX=0 NormalY=0 NormalZ=1 AngleXU=0 Radius=2.75
  constraints (26):
    c: Coincident(g0,g1)
    c: Coincident(g1,g2)
    c: Coincident(g2,g3)
    c: Coincident(g3,g0)
    c: Horizontal(g0)
    c: Horizontal(g2)
    c: Vertical(g1)
    c: Vertical(g3)
    c: Coincident(g0,g-3)
    c: Coincident(g1,g-4)
    c: Coincident(g4,g5)
    c: Coincident(g5,g6)
    c: Coincident(g6,g7)
    c: Coincident(g7,g4)
    c: Horizontal(g4)
    c: Horizontal(g6)
    c: Vertical(g5)
    c: Vertical(g7)
    c: Coincident(g4,g-5)
    c: Coincident(g5,g-6)
    c: DistanceX(g0,g8) = 10.05
    c: DistanceX(g9,g4) = 10.05
    c: DistanceY(g9,g4) = 10.05
    c: DistanceY(g8,g0) = 10.05
    c: Diameter(g8) = 5.5
    c: Equal(g8,g9)
FEATURE [PartDesign::Pad] Pad028
  BaseFeature = -> Pocket022
  Length = 2.8
  Length2 = 100
  Profile = -> Sketch051
  Reversed = true
  Type = 0
  expr: Length = Spreadsheet006.wall
FEATURE [PartDesign::Body] Body006  label="Laptop Holder - One Slot - Closed"
  Group = -> [Sketch038,Pad020,Sketch036,Pad019,Pocket020,Sketch039,Pocket021,Fillet008,Sketch034,Pad021,Sketch033,Pocket024,Sketch040,Pocket023,Fillet009,Sketch037,Pad022,Pad018,Sketch041,Pocket025,Sketch035,Pocket022,Sketch051,Pad028]
  Origin = -> Origin006
  Placement = pos=(1000,0,40) rot=(0,0,1;0rad)
  Tip = -> Pad028
FEATURE [Sketcher::SketchObject] Sketch052
  ExternalGeometry = -> [Pocket030]
  MapMode = 5
  Placement = pos=(0,0,6) rot=(0,0,1;0rad)
  Support = -> [Pocket030]
  expr: Constraints[24] = Spreadsheet007.fixholedia
  expr: Constraints[23] = Spreadsheet007.extrusion / 2
  expr: Constraints[22] = Spreadsheet007.extrusion / 2
  expr: Constraints[21] = Spreadsheet007.extrusion / 2
  expr: Constraints[20] = Spreadsheet007.extrusion / 2
  sketch-geometry (10):
    g0: LineSegment StartX=2.8 StartY=22.9 StartZ=0 EndX=22.9 EndY=22.9 EndZ=0
    g1: LineSegment StartX=22.9 StartY=22.9 StartZ=0 EndX=22.9 EndY=2.8 EndZ=0
    g2: LineSegment StartX=22.9 StartY=2.8 StartZ=0 EndX=2.8 EndY=2.8 EndZ=0
    g3: LineSegment StartX=2.8 StartY=2.8 StartZ=0 EndX=2.8 EndY=22.9 EndZ=0
    g4: LineSegment StartX=82.9 StartY=2.8 StartZ=0 EndX=103 EndY=2.8 EndZ=0
    g5: LineSegment StartX=103 StartY=2.8 StartZ=0 EndX=103 EndY=22.9 EndZ=0
    g6: LineSegment StartX=103 StartY=22.9 StartZ=0 EndX=82.9 EndY=22.9 EndZ=0
    g7: LineSegment StartX=82.9 StartY=22.9 StartZ=0 EndX=82.9 EndY=2.8 EndZ=0
    g8: Circle CenterX=92.95 CenterY=12.85 CenterZ=0 NormalX=0 NormalY=0 NormalZ=1 AngleXU=0 Radius=2.75
    g9: Circle CenterX=12.85 CenterY=12.85 CenterZ=0 NormalX=0 NormalY=0 NormalZ=1 AngleXU=0 Radius=2.75
  constraints (26):
    c: Coincident(g0,g1)
    c: Coincident(g1,g2)
    c: Coincident(g2,g3)
    c: Coincident(g3,g0)
    c: Horizontal(g0)
    c: Horizontal(g2)
    c: Vertical(g1)
    c: Vertical(g3)
    c: Coincident(g0,g-7)
    c: Coincident(g1,g-8)
    c: Coincident(g4,g5)
    c: Coincident(g5,g6)
    c: Coincident(g6,g7)
    c: Coincident(g7,g4)
    c: Horizontal(g4)
    c: Horizontal(g6)
    c: Vertical(g5)
    c: Vertical(g7)
    c: Coincident(g4,g-5)
    c: Coincident(g5,g-4)
    c: DistanceY(g9,g0) = 10.05
    c: DistanceY(g8,g6) = 10.05
    c: DistanceX(g0,g9) = 10.05
    c: DistanceX(g6,g8) = 10.05
    c: Diameter(g9) = 5.5
    c: Equal(g9,g8)
FEATURE [PartDesign::Pad] Pad029
  BaseFeature = -> Pocket030
  Length = 2.8
  Length2 = 100
  Profile = -> Sketch052
  Reversed = true
  Type = 0
  expr: Length = Spreadsheet007.wall
FEATURE [PartDesign::Body] Body007  label="Laptop Holder - Two Slots - Closed"
  Group = -> [Sketch047,Pad026,Sketch043,Pad027,Pocket028,Sketch050,Pocket026,Fillet011,Sketch049,Pad023,Sketch045,Pocket031,Sketch042,Pocket029,Fillet010,Sketch046,Pad024,Pad025,Sketch048,Pocket027,Sketch044,Pocket030,Sketch052,Pad029]
  Origin = -> Origin007
  Placement = pos=(800,0,40) rot=(0,0,1;0rad)
  Tip = -> Pad029
FEATURE [TechDraw::DrawSVGTemplate] Template
  EditableTexts = Designed_by_Name=Daniel; FC-Date=July 18th, 2020; FC-SC=1 : 0.8; FC-SH=1/1; FC-Title=Laptop Holder - One Slot; Subtitle=License - CC BY-NC-SA
  Height = 210
  Orientation = 1
  Width = 297
FEATURE [TechDraw::DrawSVGTemplate] Template001
  EditableTexts = Designed_by_Name=Daniel; FC-Date=July 18th, 2020; FC-SC=1 : 0.8; FC-SH=1/1; FC-Title=Laptop Holder - Two Slots; Subtitle=License - CC BY-NC-SA
  Height = 210
  Orientation = 1
  Width = 297
FEATURE [TechDraw::DrawViewPart] View
  CoarseView = false
  Direction = (0,0,-1)
  Focus = 100
  HardHidden = false
  IsoCount = 0
  IsoHidden = false
  IsoVisible = false
  LockPosition = false
  Perspective = false
  Rotation = 0
  Scale = 0.8
  ScaleType = 0
  SeamHidden = false
  SeamVisible = true
  SmoothHidden = false
  SmoothVisible = true
  Source = -> [Body006]
  X = 212.591
  XDirection = (1,0,0)
  Y = 132.955
FEATURE [TechDraw::DrawViewPart] View001
  CoarseView = false
  Direction = (0,0,-1)
  Focus = 100
  HardHidden = false
  IsoCount = 0
  IsoHidden = false
  IsoVisible = false
  LockPosition = false
  Perspective = false
  Rotation = 0
  Scale = 0.8
  ScaleType = 0
  SeamHidden = false
  SeamVisible = true
  SmoothHidden = false
  SmoothVisible = true
  Source = -> [Body007]
  X = 218.5
  XDirection = (1,0,0)
  Y = 128.636
FEATURE [TechDraw::DrawViewPart] View002
  CoarseView = false
  Direction = (-1,0,0)
  Focus = 100
  HardHidden = false
  IsoCount = 0
  IsoHidden = false
  IsoVisible = false
  LockPosition = false
  Perspective = false
  Rotation = 0
  Scale = 0.8
  ScaleType = 0
  SeamHidden = false
  SeamVisible = true
  SmoothHidden = false
  SmoothVisible = true
  Source = -> [Body007]
  X = 78.0455
  XDirection = (0,1,0)
  Y = 57.7273
FEATURE [TechDraw::DrawViewPart] View003
  CoarseView = false
  Direction = (-1,0,0)
  Focus = 100
  HardHidden = false
  IsoCount = 0
  IsoHidden = false
  IsoVisible = false
  LockPosition = false
  Perspective = false
  Rotation = 0
  Scale = 0.8
  ScaleType = 0
  SeamHidden = false
  SeamVisible = true
  SmoothHidden = false
  SmoothVisible = true
  Source = -> [Body006]
  X = 78.5
  XDirection = (0,1,0)
  Y = 56.1364
FEATURE [TechDraw::DrawViewPart] View004
  CoarseView = false
  Direction = (0,-1,0)
  Focus = 100
  HardHidden = false
  IsoCount = 0
  IsoHidden = false
  IsoVisible = false
  LockPosition = false
  Perspective = false
  Rotation = 0
  Scale = 0.8
  ScaleType = 0
  SeamHidden = false
  SeamVisible = true
  SmoothHidden = false
  SmoothVisible = true
  Source = -> [Body007]
  X = 82.8182
  XDirection = (-1,0,0)
  Y = 135.455
FEATURE [TechDraw::DrawViewPart] View005
  CoarseView = false
  Direction = (0,-1,0)
  Focus = 100
  HardHidden = false
  IsoCount = 0
  IsoHidden = false
  IsoVisible = false
  LockPosition = false
  Perspective = false
  Rotation = 0
  Scale = 0.8
  ScaleType = 0
  SeamHidden = false
  SeamVisible = true
  SmoothHidden = false
  SmoothVisible = true
  Source = -> [Body006]
  X = 82.3636
  XDirection = (-1,0,0)
  Y = 137.273
FEATURE [TechDraw::DrawViewDimension] Dimension
  Arbitrary = false
  FormatSpec = %.2f
  Inverted = false
  LockPosition = false
  MeasureType = 1
  OverTolerance = 0
  References2D = -> [View001]
  Rotation = 0
  Scale = 0.8
  ScaleType = 0
  TheoreticalExact = false
  Type = 2
  UnderTolerance = 0
  X = 58.815
  Y = -14.0798
FEATURE [TechDraw::DrawViewDimension] Dimension001
  Arbitrary = false
  FormatSpec = %.2f
  Inverted = false
  LockPosition = false
  MeasureType = 1
  OverTolerance = 0
  References2D = -> [View001]
  Rotation = 0
  Scale = 0.8
  ScaleType = 0
  TheoreticalExact = false
  Type = 2
  UnderTolerance = 0
  X = -62.7759
  Y = -59.1744
FEATURE [TechDraw::DrawViewDimension] Dimension002
  Arbitrary = false
  FormatSpec = %.2f
  Inverted = false
  LockPosition = false
  MeasureType = 1
  OverTolerance = 0
  References2D = -> [View001]
  Rotation = 0
  Scale = 0.8
  ScaleType = 0
  TheoreticalExact = false
  Type = 2
  UnderTolerance = 0
  X = -20.3859
  Y = -60.3053
FEATURE [TechDraw::DrawViewDimension] Dimension003
  Arbitrary = false
  FormatSpec = %.2f
  Inverted = false
  LockPosition = false
  MeasureType = 1
  OverTolerance = 0
  References2D = -> [View001]
  Rotation = 0
  Scale = 0.8
  ScaleType = 0
  TheoreticalExact = false
  Type = 2
  UnderTolerance = 0
  X = -27.3155
  Y = -60.5816
FEATURE [TechDraw::DrawViewDimension] Dimension004
  Arbitrary = false
  FormatSpec = %.2f
  Inverted = false
  LockPosition = false
  MeasureType = 1
  OverTolerance = 0
  References2D = -> [View001]
  Rotation = 0
  Scale = 0.8
  ScaleType = 0
  TheoreticalExact = false
  Type = 2
  UnderTolerance = 0
  X = -34.1336
  Y = -60.4944
FEATURE [TechDraw::DrawViewDimension] Dimension005
  Arbitrary = false
  FormatSpec = ⌀%.2f
  Inverted = false
  LockPosition = false
  MeasureType = 1
  OverTolerance = 0
  References2D = -> [View001]
  Rotation = 0
  Scale = 0.8
  ScaleType = 0
  TheoreticalExact = false
  Type = 5
  UnderTolerance = 0
  X = 19.5455
  Y = 34.0909
FEATURE [TechDraw::DrawViewDimension] Dimension006
  Arbitrary = false
  FormatSpec = %.2f
  Inverted = false
  LockPosition = false
  MeasureType = 1
  OverTolerance = 0
  References2D = -> [View001]
  Rotation = 0
  Scale = 0.8
  ScaleType = 0
  TheoreticalExact = false
  Type = 6
  UnderTolerance = 0
  X = -0.909091
  Y = 43.1818
FEATURE [TechDraw::DrawViewDimension] Dimension007
  Arbitrary = false
  FormatSpec = ⌀%.2f
  Inverted = false
  LockPosition = false
  MeasureType = 1
  OverTolerance = 0
  References2D = -> [View001]
  Rotation = 0
  Scale = 0.8
  ScaleType = 0
  TheoreticalExact = false
  Type = 5
  UnderTolerance = 0
  X = -16.8182
  Y = -7.04545
FEATURE [TechDraw::DrawViewDimension] Dimension009
  Arbitrary = false
  FormatSpec = ⌀%.2f
  Inverted = false
  LockPosition = false
  MeasureType = 1
  OverTolerance = 0
  References2D = -> [View002]
  Rotation = 0
  Scale = 0.8
  ScaleType = 0
  TheoreticalExact = false
  Type = 5
  UnderTolerance = 0
  X = 7.04545
  Y = -4.77273
FEATURE [TechDraw::DrawViewDimension] Dimension010
  Arbitrary = false
  FormatSpec = ⌀%.2f
  Inverted = false
  LockPosition = false
  MeasureType = 1
  OverTolerance = 0
  References2D = -> [View004]
  Rotation = 0
  Scale = 0.8
  ScaleType = 0
  TheoreticalExact = false
  Type = 5
  UnderTolerance = 0
  X = -38.8636
  Y = -4.09091
FEATURE [TechDraw::DrawViewDimension] Dimension012
  Arbitrary = false
  FormatSpec = %.2f
  Inverted = false
  LockPosition = false
  MeasureType = 1
  OverTolerance = 0
  References2D = -> [View002]
  Rotation = 0
  Scale = 0.8
  ScaleType = 0
  TheoreticalExact = false
  Type = 2
  UnderTolerance = 0
  X = -57.978
  Y = -28.0091
FEATURE [TechDraw::DrawViewDimension] Dimension013
  Arbitrary = false
  FormatSpec = %.2f
  Inverted = false
  LockPosition = false
  MeasureType = 1
  OverTolerance = 0
  References2D = -> [View002]
  Rotation = 0
  Scale = 0.8
  ScaleType = 0
  TheoreticalExact = false
  Type = 2
  UnderTolerance = 0
  X = -30.0438
  Y = -7.29091
FEATURE [TechDraw::DrawViewDimension] Dimension014
  Arbitrary = false
  FormatSpec = %.2f
  Inverted = false
  LockPosition = false
  MeasureType = 1
  OverTolerance = 0
  References2D = -> [View002]
  Rotation = 0
  Scale = 0.8
  ScaleType = 0
  TheoreticalExact = false
  Type = 2
  UnderTolerance = 0
  X = 54.3416
  Y = -29.3636
FEATURE [TechDraw::DrawViewDimension] Dimension015
  Arbitrary = false
  FormatSpec = %.2f
  Inverted = false
  LockPosition = false
  MeasureType = 1
  OverTolerance = 0
  References2D = -> [View002]
  Rotation = 0
  Scale = 0.8
  ScaleType = 0
  TheoreticalExact = false
  Type = 2
  UnderTolerance = 0
  X = 59.3416
  Y = 5.36364
FEATURE [TechDraw::DrawViewDimension] Dimension016
  Arbitrary = false
  FormatSpec = %.2f
  Inverted = false
  LockPosition = false
  MeasureType = 1
  OverTolerance = 0
  References2D = -> [View002]
  Rotation = 0
  Scale = 0.8
  ScaleType = 0
  TheoreticalExact = false
  Type = 1
  UnderTolerance = 0
  X = 43.038
  Y = 7.81818
FEATURE [TechDraw::DrawViewDimension] Dimension017
  Arbitrary = false
  FormatSpec = %.2f
  Inverted = false
  LockPosition = false
  MeasureType = 1
  OverTolerance = 0
  References2D = -> [View002]
  Rotation = 0
  Scale = 0.8
  ScaleType = 0
  TheoreticalExact = false
  Type = 1
  UnderTolerance = 0
  X = 28.398
  Y = 14.9545
FEATURE [TechDraw::DrawViewDimension] Dimension018
  Arbitrary = false
  FormatSpec = %.2f
  Inverted = false
  LockPosition = false
  MeasureType = 1
  OverTolerance = 0
  References2D = -> [View002]
  Rotation = 0
  Scale = 0.8
  ScaleType = 0
  TheoreticalExact = false
  Type = 1
  UnderTolerance = 0
  X = 9.358
  Y = 39.0455
FEATURE [TechDraw::DrawViewDimension] Dimension019
  Arbitrary = false
  FormatSpec = %.2f
  Inverted = false
  LockPosition = false
  MeasureType = 1
  OverTolerance = 0
  References2D = -> [View002]
  Rotation = 0
  Scale = 0.8
  ScaleType = 0
  TheoreticalExact = false
  Type = 1
  UnderTolerance = 0
  X = 9.218
  Y = 33.5909
FEATURE [TechDraw::DrawViewDimension] Dimension020
  Arbitrary = false
  FormatSpec = %.2f
  Inverted = false
  LockPosition = false
  MeasureType = 1
  OverTolerance = 0
  References2D = -> [View002]
  Rotation = 0
  Scale = 0.8
  ScaleType = 0
  TheoreticalExact = false
  Type = 1
  UnderTolerance = 0
  X = 9.16891
  Y = 27.9091
FEATURE [TechDraw::DrawViewDimension] Dimension021
  Arbitrary = false
  FormatSpec = %.2f
  Inverted = false
  LockPosition = false
  MeasureType = 1
  OverTolerance = 0
  References2D = -> [View002]
  Rotation = 0
  Scale = 0.8
  ScaleType = 0
  TheoreticalExact = false
  Type = 1
  UnderTolerance = 0
  X = -6.79291
  Y = 6.70909
FEATURE [TechDraw::DrawViewDimension] Dimension022
  Arbitrary = false
  FormatSpec = %.2f
  Inverted = false
  LockPosition = false
  MeasureType = 1
  OverTolerance = 0
  References2D = -> [View002]
  Rotation = 0
  Scale = 0.8
  ScaleType = 0
  TheoreticalExact = false
  Type = 1
  UnderTolerance = 0
  X = -12.5782
  Y = -26.3182
FEATURE [TechDraw::DrawViewDimension] Dimension023
  Arbitrary = false
  FormatSpec = %.2f
  Inverted = false
  LockPosition = false
  MeasureType = 1
  OverTolerance = 0
  References2D = -> [View002]
  Rotation = 0
  Scale = 0.8
  ScaleType = 0
  TheoreticalExact = false
  Type = 1
  UnderTolerance = 0
  X = 35.8544
  Y = -26.3182
FEATURE [TechDraw::DrawViewDimension] Dimension024
  Arbitrary = false
  FormatSpec = %.2f
  Inverted = false
  LockPosition = false
  MeasureType = 1
  OverTolerance = 0
  References2D = -> [View004]
  Rotation = 0
  Scale = 0.8
  ScaleType = 0
  TheoreticalExact = false
  Type = 1
  UnderTolerance = 0
  X = -0.227273
  Y = -26.5455
FEATURE [TechDraw::DrawViewDimension] Dimension025
  Arbitrary = false
  FormatSpec = %.2f
  Inverted = false
  LockPosition = false
  MeasureType = 1
  OverTolerance = 0
  References2D = -> [View004]
  Rotation = 0
  Scale = 0.8
  ScaleType = 0
  TheoreticalExact = false
  Type = 1
  UnderTolerance = 0
  X = 0.681818
  Y = 40.5455
FEATURE [TechDraw::DrawViewDimension] Dimension026
  Arbitrary = false
  FormatSpec = %.2f
  Inverted = false
  LockPosition = false
  MeasureType = 1
  OverTolerance = 0
  References2D = -> [View004]
  Rotation = 0
  Scale = 0.8
  ScaleType = 0
  TheoreticalExact = false
  Type = 1
  UnderTolerance = 0
  X = 0.454545
  Y = 30.4091
FEATURE [TechDraw::DrawViewDimension] Dimension027
  Arbitrary = false
  FormatSpec = %.2f
  Inverted = false
  LockPosition = false
  MeasureType = 1
  OverTolerance = 0
  References2D = -> [View004]
  Rotation = 0
  Scale = 0.8
  ScaleType = 0
  TheoreticalExact = false
  Type = 2
  UnderTolerance = 0
  X = 9.26
  Y = 1.57273
FEATURE [TechDraw::DrawViewDimension] Dimension028
  Arbitrary = false
  FormatSpec = %.2f
  Inverted = false
  LockPosition = false
  MeasureType = 1
  OverTolerance = 0
  References2D = -> [View004]
  Rotation = 0
  Scale = 0.8
  ScaleType = 0
  TheoreticalExact = false
  Type = 1
  UnderTolerance = 0
  X = 30.6764
  Y = 8.52727
FEATURE [TechDraw::DrawViewDimension] Dimension029
  Arbitrary = false
  FormatSpec = %.2f
  Inverted = false
  LockPosition = false
  MeasureType = 1
  OverTolerance = 0
  References2D = -> [View004]
  Rotation = 0
  Scale = 0.8
  ScaleType = 0
  TheoreticalExact = false
  Type = 2
  UnderTolerance = 0
  X = 2.32
  Y = -1.19091
FEATURE [TechDraw::DrawViewDimension] Dimension030
  Arbitrary = false
  FormatSpec = %.2f
  Inverted = false
  LockPosition = false
  MeasureType = 1
  OverTolerance = 0
  References2D = -> [View004]
  Rotation = 0
  Scale = 0.8
  ScaleType = 0
  TheoreticalExact = false
  Type = 2
  UnderTolerance = 0
  X = 59.7743
  Y = -28.2273
FEATURE [TechDraw::DrawViewDimension] Dimension031
  Arbitrary = false
  FormatSpec = %.2f
  Inverted = false
  LockPosition = false
  MeasureType = 1
  OverTolerance = 0
  References2D = -> [View004]
  Rotation = 0
  Scale = 0.8
  ScaleType = 0
  TheoreticalExact = false
  Type = 2
  UnderTolerance = 0
  X = 55.9548
  Y = 11.7273
FEATURE [TechDraw::DrawViewDimension] Dimension032
  Arbitrary = false
  FormatSpec = %.2f
  Inverted = false
  LockPosition = false
  MeasureType = 1
  OverTolerance = 0
  References2D = -> [View001]
  Rotation = 0
  Scale = 0.8
  ScaleType = 0
  TheoreticalExact = false
  Type = 1
  UnderTolerance = 0
  X = 32.04
  Y = 5.53109
FEATURE [TechDraw::DrawViewDimension] Dimension033
  Arbitrary = false
  FormatSpec = %.2f
  Inverted = false
  LockPosition = false
  MeasureType = 1
  OverTolerance = 0
  References2D = -> [View001]
  Rotation = 0
  Scale = 0.8
  ScaleType = 0
  TheoreticalExact = false
  Type = 2
  UnderTolerance = 0
  X = 47.1255
  Y = -10.6907
FEATURE [TechDraw::DrawViewDimension] Dimension034
  Arbitrary = false
  FormatSpec = %.2f
  Inverted = false
  LockPosition = false
  MeasureType = 1
  OverTolerance = 0
  References2D = -> [View001]
  Rotation = 0
  Scale = 0.8
  ScaleType = 0
  TheoreticalExact = false
  Type = 1
  UnderTolerance = 0
  X = 32.2673
  Y = 12.1438
FEATURE [TechDraw::DrawViewDimension] Dimension035
  Arbitrary = false
  FormatSpec = %.2f
  Inverted = false
  LockPosition = false
  MeasureType = 1
  OverTolerance = 0
  References2D = -> [View001]
  Rotation = 0
  Scale = 0.8
  ScaleType = 0
  TheoreticalExact = false
  Type = 2
  UnderTolerance = 0
  X = -39.2436
  Y = 8.92382
FEATURE [TechDraw::DrawViewDimension] Dimension037
  Arbitrary = false
  FormatSpec = ⌀%.2f
  Inverted = false
  LockPosition = false
  MeasureType = 1
  OverTolerance = 0
  References2D = -> [View001]
  Rotation = 0
  Scale = 0.8
  ScaleType = 0
  TheoreticalExact = false
  Type = 5
  UnderTolerance = 0
  X = -21.1364
  Y = 35
FEATURE [TechDraw::DrawViewDimension] Dimension038
  Arbitrary = false
  FormatSpec = %.2f
  Inverted = false
  LockPosition = false
  MeasureType = 1
  OverTolerance = 0
  References2D = -> [View001]
  Rotation = 0
  Scale = 0.8
  ScaleType = 0
  TheoreticalExact = false
  Type = 1
  UnderTolerance = 0
  X = 0.609091
  Y = -30.6907
FEATURE [TechDraw::DrawViewDimension] Dimension039
  Arbitrary = false
  FormatSpec = %.2f
  Inverted = false
  LockPosition = false
  MeasureType = 1
  OverTolerance = 0
  References2D = -> [View001]
  Rotation = 0
  Scale = 0.8
  ScaleType = 0
  TheoreticalExact = false
  Type = 1
  UnderTolerance = 0
  X = -49.6091
  Y = -11.9307
FEATURE [TechDraw::DrawViewDimension] Dimension040
  Arbitrary = false
  FormatSpec = %.2f
  Inverted = false
  LockPosition = false
  MeasureType = 1
  OverTolerance = 0
  References2D = -> [View001]
  Rotation = 0
  Scale = 0.8
  ScaleType = 0
  TheoreticalExact = false
  Type = 2
  UnderTolerance = 0
  X = -59.0191
  Y = 18.4076
FEATURE [TechDraw::DrawViewDimension] Dimension041
  Arbitrary = false
  FormatSpec = %.2f
  Inverted = false
  LockPosition = false
  MeasureType = 1
  OverTolerance = 0
  References2D = -> [View001]
  Rotation = 0
  Scale = 0.8
  ScaleType = 0
  TheoreticalExact = false
  Type = 1
  UnderTolerance = 0
  X = 0.227273
  Y = -23.958
FEATURE [TechDraw::DrawPage] Page001  label="Dimensions Laptop Holder - Two Slots"
  KeepUpdated = true
  NextBalloonIndex = 1
  ProjectionType = 0
  Scale = 0.8
  Template = -> Template001
  Views = -> [View001,View002,View004,Dimension,Dimension001,Dimension002,Dimension003,Dimension004,Dimension005,Dimension006,Dimension007,Dimension009,Dimension010,Dimension012,Dimension013,Dimension014,Dimension015,Dimension016,Dimension017,Dimension018,Dimension019,Dimension020,Dimension021,Dimension022,Dimension023,Dimension024,Dimension025,Dimension026,Dimension027,Dimension028,Dimension029,Dimension030,+10 more]
FEATURE [TechDraw::DrawViewDimension] Dimension042
  Arbitrary = false
  FormatSpec = %.2f
  Inverted = false
  LockPosition = false
  MeasureType = 1
  OverTolerance = 0
  References2D = -> [View]
  Rotation = 0
  Scale = 0.8
  ScaleType = 0
  TheoreticalExact = false
  Type = 6
  UnderTolerance = 0
  X = -0.454545
  Y = 33.6364
FEATURE [TechDraw::DrawViewDimension] Dimension043
  Arbitrary = false
  FormatSpec = ⌀%.2f
  Inverted = false
  LockPosition = false
  MeasureType = 1
  OverTolerance = 0
  References2D = -> [View]
  Rotation = 0
  Scale = 0.8
  ScaleType = 0
  TheoreticalExact = false
  Type = 5
  UnderTolerance = 0
  X = 19.3182
  Y = 27.9545
FEATURE [TechDraw::DrawViewDimension] Dimension044
  Arbitrary = false
  FormatSpec = ⌀%.2f
  Inverted = false
  LockPosition = false
  MeasureType = 1
  OverTolerance = 0
  References2D = -> [View]
  Rotation = 0
  Scale = 0.8
  ScaleType = 0
  TheoreticalExact = false
  Type = 5
  UnderTolerance = 0
  X = -22.0455
  Y = 28.6364
FEATURE [TechDraw::DrawViewDimension] Dimension045
  Arbitrary = false
  FormatSpec = %.2f
  Inverted = false
  LockPosition = false
  MeasureType = 1
  OverTolerance = 0
  References2D = -> [View]
  Rotation = 0
  Scale = 0.8
  ScaleType = 0
  TheoreticalExact = false
  Type = 2
  UnderTolerance = 0
  X = -54.8973
  Y = 10.9513
FEATURE [TechDraw::DrawViewDimension] Dimension046
  Arbitrary = false
  FormatSpec = %.2f
  Inverted = false
  LockPosition = false
  MeasureType = 1
  OverTolerance = 0
  References2D = -> [View]
  Rotation = 0
  Scale = 0.8
  ScaleType = 0
  TheoreticalExact = false
  Type = 2
  UnderTolerance = 0
  X = -40.1182
  Y = 1.24018
FEATURE [TechDraw::DrawViewDimension] Dimension047
  Arbitrary = false
  FormatSpec = %.2f
  Inverted = false
  LockPosition = false
  MeasureType = 1
  OverTolerance = 0
  References2D = -> [View]
  Rotation = 0
  Scale = 0.8
  ScaleType = 0
  TheoreticalExact = false
  Type = 1
  UnderTolerance = 0
  X = -48.0182
  Y = -18.2507
FEATURE [TechDraw::DrawViewDimension] Dimension048
  Arbitrary = false
  FormatSpec = ⌀%.2f
  Inverted = false
  LockPosition = false
  MeasureType = 1
  OverTolerance = 0
  References2D = -> [View]
  Rotation = 0
  Scale = 0.8
  ScaleType = 0
  TheoreticalExact = false
  Type = 5
  UnderTolerance = 0
  X = -15.6818
  Y = -13.6364
FEATURE [TechDraw::DrawViewDimension] Dimension049
  Arbitrary = false
  FormatSpec = %.2f
  Inverted = false
  LockPosition = false
  MeasureType = 1
  OverTolerance = 0
  References2D = -> [View]
  Rotation = 0
  Scale = 0.8
  ScaleType = 0
  TheoreticalExact = false
  Type = 1
  UnderTolerance = 0
  X = 41.2909
  Y = -32.9198
FEATURE [TechDraw::DrawViewDimension] Dimension050
  Arbitrary = false
  FormatSpec = %.2f
  Inverted = false
  LockPosition = false
  MeasureType = 1
  OverTolerance = 0
  References2D = -> [View]
  Rotation = 0
  Scale = 0.8
  ScaleType = 0
  TheoreticalExact = false
  Type = 1
  UnderTolerance = 0
  X = 0.227273
  Y = -30.278
FEATURE [TechDraw::DrawViewDimension] Dimension051
  Arbitrary = false
  FormatSpec = %.2f
  Inverted = false
  LockPosition = false
  MeasureType = 1
  OverTolerance = 0
  References2D = -> [View]
  Rotation = 0
  Scale = 0.8
  ScaleType = 0
  TheoreticalExact = false
  Type = 1
  UnderTolerance = 0
  X = 39.9945
  Y = 7.18746
FEATURE [TechDraw::DrawViewDimension] Dimension052
  Arbitrary = false
  FormatSpec = %.2f
  Inverted = false
  LockPosition = false
  MeasureType = 1
  OverTolerance = 0
  References2D = -> [View]
  Rotation = 0
  Scale = 0.8
  ScaleType = 0
  TheoreticalExact = false
  Type = 1
  UnderTolerance = 0
  X = 34.3127
  Y = 0.120184
FEATURE [TechDraw::DrawViewDimension] Dimension053
  Arbitrary = false
  FormatSpec = %.2f
  Inverted = false
  LockPosition = false
  MeasureType = 1
  OverTolerance = 0
  References2D = -> [View]
  Rotation = 0
  Scale = 0.8
  ScaleType = 0
  TheoreticalExact = false
  Type = 2
  UnderTolerance = 0
  X = 46.2164
  Y = -16.5562
FEATURE [TechDraw::DrawViewDimension] Dimension054
  Arbitrary = false
  FormatSpec = %.2f
  Inverted = false
  LockPosition = false
  MeasureType = 1
  OverTolerance = 0
  References2D = -> [View]
  Rotation = 0
  Scale = 0.8
  ScaleType = 0
  TheoreticalExact = false
  Type = 2
  UnderTolerance = 0
  X = 61.185
  Y = -34.9453
FEATURE [TechDraw::DrawViewDimension] Dimension055
  Arbitrary = false
  FormatSpec = %.2f
  Inverted = false
  LockPosition = false
  MeasureType = 1
  OverTolerance = 0
  References2D = -> [View]
  Rotation = 0
  Scale = 0.8
  ScaleType = 0
  TheoreticalExact = false
  Type = 2
  UnderTolerance = 0
  X = -40.1586
  Y = -55.7162
FEATURE [TechDraw::DrawViewDimension] Dimension056
  Arbitrary = false
  FormatSpec = %.2f
  Inverted = false
  LockPosition = false
  MeasureType = 1
  OverTolerance = 0
  References2D = -> [View]
  Rotation = 0
  Scale = 0.8
  ScaleType = 0
  TheoreticalExact = false
  Type = 2
  UnderTolerance = 0
  X = -46.8609
  Y = -55.3107
FEATURE [TechDraw::DrawViewDimension] Dimension057
  Arbitrary = false
  FormatSpec = %.2f
  Inverted = false
  LockPosition = false
  MeasureType = 1
  OverTolerance = 0
  References2D = -> [View]
  Rotation = 0
  Scale = 0.8
  ScaleType = 0
  TheoreticalExact = false
  Type = 2
  UnderTolerance = 0
  X = 56.3525
  Y = -14.5271
FEATURE [TechDraw::DrawViewDimension] Dimension058
  Arbitrary = false
  FormatSpec = %.2f
  Inverted = false
  LockPosition = false
  MeasureType = 1
  OverTolerance = 0
  References2D = -> [View005]
  Rotation = 0
  Scale = 0.8
  ScaleType = 0
  TheoreticalExact = false
  Type = 1
  UnderTolerance = 0
  X = -3.18182
  Y = -27.4545
FEATURE [TechDraw::DrawViewDimension] Dimension059
  Arbitrary = false
  FormatSpec = %.2f
  Inverted = false
  LockPosition = false
  MeasureType = 1
  OverTolerance = 0
  References2D = -> [View005]
  Rotation = 0
  Scale = 0.8
  ScaleType = 0
  TheoreticalExact = false
  Type = 1
  UnderTolerance = 0
  X = 0
  Y = 40.5455
FEATURE [TechDraw::DrawViewDimension] Dimension060
  Arbitrary = false
  FormatSpec = %.2f
  Inverted = false
  LockPosition = false
  MeasureType = 1
  OverTolerance = 0
  References2D = -> [View005]
  Rotation = 0
  Scale = 0.8
  ScaleType = 0
  TheoreticalExact = false
  Type = 1
  UnderTolerance = 0
  X = 0.227273
  Y = 30.4091
FEATURE [TechDraw::DrawViewDimension] Dimension061
  Arbitrary = false
  FormatSpec = %.2f
  Inverted = false
  LockPosition = false
  MeasureType = 1
  OverTolerance = 0
  References2D = -> [View005]
  Rotation = 0
  Scale = 0.8
  ScaleType = 0
  TheoreticalExact = false
  Type = 1
  UnderTolerance = 0
  X = 32.7218
  Y = 3.75454
FEATURE [TechDraw::DrawViewDimension] Dimension062
  Arbitrary = false
  FormatSpec = %.2f
  Inverted = false
  LockPosition = false
  MeasureType = 1
  OverTolerance = 0
  References2D = -> [View005]
  Rotation = 0
  Scale = 0.8
  ScaleType = 0
  TheoreticalExact = false
  Type = 2
  UnderTolerance = 0
  X = 61.138
  Y = -28.4545
FEATURE [TechDraw::DrawViewDimension] Dimension063
  Arbitrary = false
  FormatSpec = %.2f
  Inverted = false
  LockPosition = false
  MeasureType = 1
  OverTolerance = 0
  References2D = -> [View005]
  Rotation = 0
  Scale = 0.8
  ScaleType = 0
  TheoreticalExact = false
  Type = 2
  UnderTolerance = 0
  X = 58.2275
  Y = 9.68182
FEATURE [TechDraw::DrawViewDimension] Dimension064
  Arbitrary = false
  FormatSpec = %.2f
  Inverted = false
  LockPosition = false
  MeasureType = 1
  OverTolerance = 0
  References2D = -> [View005]
  Rotation = 0
  Scale = 0.8
  ScaleType = 0
  TheoreticalExact = false
  Type = 2
  UnderTolerance = 0
  X = 7.47557
  Y = 0.400001
FEATURE [TechDraw::DrawViewDimension] Dimension065
  Arbitrary = false
  FormatSpec = %.2f
  Inverted = false
  LockPosition = false
  MeasureType = 1
  OverTolerance = 0
  References2D = -> [View005]
  Rotation = 0
  Scale = 0.8
  ScaleType = 0
  TheoreticalExact = false
  Type = 2
  UnderTolerance = 0
  X = 13.8055
  Y = -0.927273
FEATURE [TechDraw::DrawViewDimension] Dimension066
  Arbitrary = false
  FormatSpec = ⌀%.2f
  Inverted = false
  LockPosition = false
  MeasureType = 1
  OverTolerance = 0
  References2D = -> [View005]
  Rotation = 0
  Scale = 0.8
  ScaleType = 0
  TheoreticalExact = false
  Type = 5
  UnderTolerance = 0
  X = -42.2727
  Y = -3.18182
FEATURE [TechDraw::DrawViewDimension] Dimension067
  Arbitrary = false
  FormatSpec = %.2f
  Inverted = false
  LockPosition = false
  MeasureType = 1
  OverTolerance = 0
  References2D = -> [View003]
  Rotation = 0
  Scale = 0.8
  ScaleType = 0
  TheoreticalExact = false
  Type = 1
  UnderTolerance = 0
  X = 16.1707
  Y = 29.2727
FEATURE [TechDraw::DrawViewDimension] Dimension068
  Arbitrary = false
  FormatSpec = %.2f
  Inverted = false
  LockPosition = false
  MeasureType = 1
  OverTolerance = 0
  References2D = -> [View003]
  Rotation = 0
  Scale = 0.8
  ScaleType = 0
  TheoreticalExact = false
  Type = 1
  UnderTolerance = 0
  X = 15.9925
  Y = 36.0909
FEATURE [TechDraw::DrawViewDimension] Dimension069
  Arbitrary = false
  FormatSpec = %.2f
  Inverted = false
  LockPosition = false
  MeasureType = 1
  OverTolerance = 0
  References2D = -> [View003]
  Rotation = 0
  Scale = 0.8
  ScaleType = 0
  TheoreticalExact = false
  Type = 1
  UnderTolerance = 0
  X = 34.9453
  Y = 8.04546
FEATURE [TechDraw::DrawViewDimension] Dimension070
  Arbitrary = false
  FormatSpec = %.2f
  Inverted = false
  LockPosition = false
  MeasureType = 1
  OverTolerance = 0
  References2D = -> [View003]
  Rotation = 0
  Scale = 0.8
  ScaleType = 0
  TheoreticalExact = false
  Type = 2
  UnderTolerance = 0
  X = 48.4762
  Y = -28.6818
FEATURE [TechDraw::DrawViewDimension] Dimension071
  Arbitrary = false
  FormatSpec = %.2f
  Inverted = false
  LockPosition = false
  MeasureType = 1
  OverTolerance = 0
  References2D = -> [View003]
  Rotation = 0
  Scale = 0.8
  ScaleType = 0
  TheoreticalExact = false
  Type = 2
  UnderTolerance = 0
  X = 52.5671
  Y = 4.22727
FEATURE [TechDraw::DrawViewDimension] Dimension072
  Arbitrary = false
  FormatSpec = %.2f
  Inverted = false
  LockPosition = false
  MeasureType = 1
  OverTolerance = 0
  References2D = -> [View003]
  Rotation = 0
  Scale = 0.8
  ScaleType = 0
  TheoreticalExact = false
  Type = 1
  UnderTolerance = 0
  X = 34.9453
  Y = -30.4091
FEATURE [TechDraw::DrawViewDimension] Dimension073
  Arbitrary = false
  FormatSpec = %.2f
  Inverted = false
  LockPosition = false
  MeasureType = 1
  OverTolerance = 0
  References2D = -> [View003]
  Rotation = 0
  Scale = 0.8
  ScaleType = 0
  TheoreticalExact = false
  Type = 1
  UnderTolerance = 0
  X = -9.89455
  Y = -30.4091
FEATURE [TechDraw::DrawViewDimension] Dimension074
  Arbitrary = false
  FormatSpec = %.2f
  Inverted = false
  LockPosition = false
  MeasureType = 1
  OverTolerance = 0
  References2D = -> [View003]
  Rotation = 0
  Scale = 0.8
  ScaleType = 0
  TheoreticalExact = false
  Type = 2
  UnderTolerance = 0
  X = -52.3398
  Y = -29.6
FEATURE [TechDraw::DrawViewDimension] Dimension075
  Arbitrary = false
  FormatSpec = %.2f
  Inverted = false
  LockPosition = false
  MeasureType = 1
  OverTolerance = 0
  References2D = -> [View003]
  Rotation = 0
  Scale = 0.8
  ScaleType = 0
  TheoreticalExact = false
  Type = 2
  UnderTolerance = 0
  X = -10.542
  Y = -3.65455
FEATURE [TechDraw::DrawViewDimension] Dimension076
  Arbitrary = false
  FormatSpec = %.2f
  Inverted = false
  LockPosition = false
  MeasureType = 1
  OverTolerance = 0
  References2D = -> [View003]
  Rotation = 0
  Scale = 0.8
  ScaleType = 0
  TheoreticalExact = false
  Type = 1
  UnderTolerance = 0
  X = -1.382
  Y = 11.7091
FEATURE [TechDraw::DrawPage] Page  label="Dimensions Laptop Holder - One Slot"
  KeepUpdated = true
  NextBalloonIndex = 1
  ProjectionType = 0
  Scale = 0.8
  Template = -> Template
  Views = -> [View,View003,View005,Dimension042,Dimension043,Dimension044,Dimension045,Dimension046,Dimension047,Dimension048,Dimension049,Dimension050,Dimension051,Dimension052,Dimension053,Dimension054,Dimension055,Dimension056,Dimension057,Dimension058,Dimension059,Dimension060,Dimension061,Dimension062,Dimension063,Dimension064,Dimension065,Dimension066,Dimension067,Dimension068,Dimension069,Dimension070,+6 more]
FEATURE [Mesh::Feature] Mesh  label="Laptop Holder - Two Slots - Closed (Meshed)"
FEATURE [Mesh::Feature] Mesh001  label="Laptop Holder - One Slot - Closed (Meshed)"
